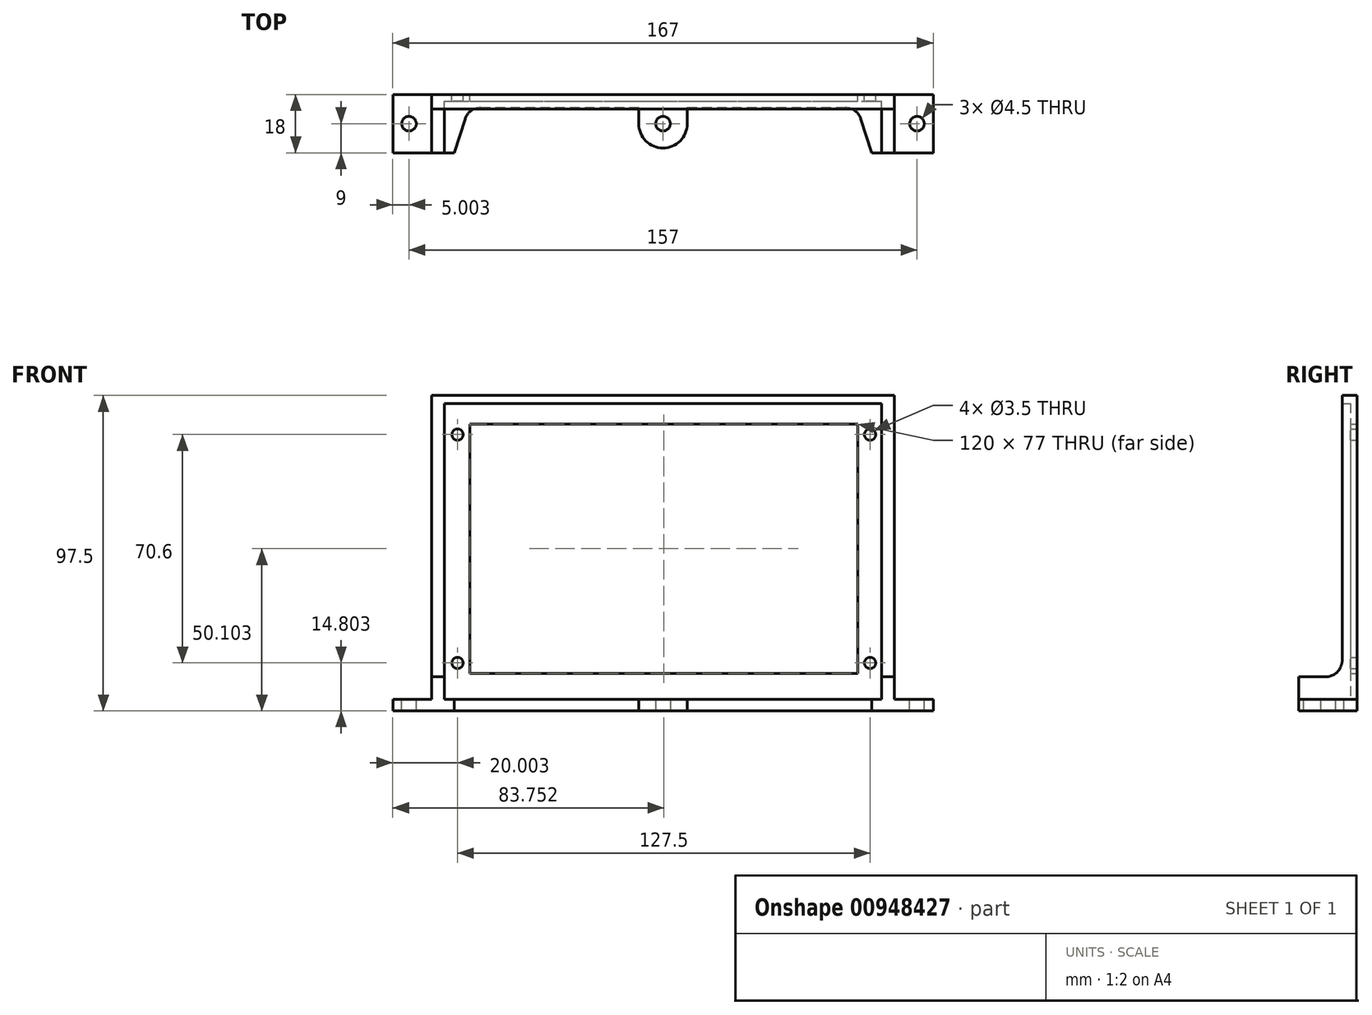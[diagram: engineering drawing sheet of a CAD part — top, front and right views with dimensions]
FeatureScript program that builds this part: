
annotation { "Feature Type Name" : "Feature", "Feature Type Description" : "" }
export const myFeature = defineFeature(function(context is Context, id is Id, definition is map)
    precondition{}
    {
        {
            var Q0;
            Q0=qCreatedBy(makeId("Front.planeOp"),FACE);
            var sketch = newSketch(context, id + "F0", { "sketchPlane" : qUnion([Q0])});
            skLineSegment(sketch, "E0.bottom", {"start": v(-17.88, 24.05) * mm, "end": v(102.12, 24.05) * mm});
            skLineSegment(sketch, "E0.top", {"start": v(-17.88, -52.95) * mm, "end": v(102.12, -52.95) * mm});
            skLineSegment(sketch, "E0.left", {"start": v(-17.88, 24.05) * mm, "end": v(-17.88, -52.95) * mm});
            skLineSegment(sketch, "E0.right", {"start": v(102.12, 24.05) * mm, "end": v(102.12, -52.95) * mm});
            skLineSegment(sketch, "E1.bottom", {"start": v(-25.63, 30.45) * mm, "end": v(109.37, 30.45) * mm});
            skLineSegment(sketch, "E1.top", {"start": v(-25.63, -59.55) * mm, "end": v(109.37, -59.55) * mm});
            skLineSegment(sketch, "E1.left", {"start": v(-25.63, 30.45) * mm, "end": v(-25.63, -59.55) * mm});
            skLineSegment(sketch, "E1.right", {"start": v(109.37, 30.45) * mm, "end": v(109.37, -59.55) * mm});
            skLineSegment(sketch, "E2.bottom", {"start": v(-21.63, 20.85) * mm, "end": v(105.87, 20.85) * mm, "construction": true});
            skLineSegment(sketch, "E2.top", {"start": v(-21.63, -49.75) * mm, "end": v(105.87, -49.75) * mm, "construction": true});
            skLineSegment(sketch, "E2.left", {"start": v(-21.63, 20.85) * mm, "end": v(-21.63, -49.75) * mm, "construction": true});
            skLineSegment(sketch, "E2.right", {"start": v(105.87, 20.85) * mm, "end": v(105.87, -49.75) * mm, "construction": true});
            skCircle(sketch, "E3", {"center": v(-21.63, 20.85) * mm, "radius": 1.75 * mm});
            skCircle(sketch, "E4", {"center": v(-21.63, -49.75) * mm, "radius": 1.75 * mm});
            skCircle(sketch, "E5", {"center": v(105.87, -49.75) * mm, "radius": 1.75 * mm});
            skCircle(sketch, "E6", {"center": v(105.87, 20.85) * mm, "radius": 1.75 * mm});
            skLineSegment(sketch, "E7.top", {"start": v(-29.63, -64.55) * mm, "end": v(113.37, -64.55) * mm});
            skLineSegment(sketch, "E8.top", {"start": v(-25.63, 30.45) * mm, "end": v(-29.63, 30.45) * mm});
            skLineSegment(sketch, "E8.left", {"start": v(-25.63, -59.55) * mm, "end": v(-25.63, 30.45) * mm});
            skLineSegment(sketch, "E8.right", {"start": v(-29.63, -64.55) * mm, "end": v(-29.63, 30.45) * mm});
            skLineSegment(sketch, "E9.bottom", {"start": v(109.37, 30.45) * mm, "end": v(113.37, 30.45) * mm});
            skLineSegment(sketch, "E9.left", {"start": v(109.37, 30.45) * mm, "end": v(109.37, -60.05) * mm});
            skLineSegment(sketch, "E9.right", {"start": v(113.37, 30.45) * mm, "end": v(113.37, -64.55) * mm});
            skPoint(sketch, "E7.right.start.orphan", {"position": v(122.02, -59.55) * mm});
            skPoint(sketch, "E10.orphan", {"position": v(-41.66, -59.55) * mm});
            skLineSegment(sketch, "E11", {"start": v(-17.88, -14.45) * mm, "end": v(102.12, -14.45) * mm, "construction": true});
            skPoint(sketch, "E12", {"position": v(-21.63, -14.45) * mm});
            skPoint(sketch, "E13", {"position": v(42.12, 20.85) * mm});
            skPoint(sketch, "E14", {"position": v(42.12, 24.05) * mm});
            skPoint(sketch, "E15", {"position": v(41.87, 30.45) * mm});
            skSolve(sketch);
        }
        {
            var Q0;
            Q0=makeQuery(id+"F0.imprint","IMPRINT",FACE,{"disambiguationData":[TD([[makeQuery(id+"F0.imprint","IMPRINT",EDGE,{"derivedFrom":sQuery(id+"F0.wireOp",EDGE,"E0.bottom")}),1.0]])]});
            extrude(context, id + "F1", {"entities" : qUnion([Q0]), "depth" : 2 * mm, "offsetDistance" : 25 * mm});
        }
        {
            var Q0;
            Q0=makeQuery(id+"F0.imprint","IMPRINT",FACE,{"disambiguationData":[TD([[makeQuery(id+"F0.imprint","IMPRINT",EDGE,{"derivedFrom":sQuery(id+"F0.wireOp",EDGE,"E8.bottom")}),-1.0]])]});
            var Q1;
            Q1=makeQuery(id+"F0.imprint","IMPRINT",FACE,{"disambiguationData":[TD([[makeQuery(id+"F0.imprint","IMPRINT",EDGE,{"derivedFrom":sQuery(id+"F0.wireOp",EDGE,"E1.top")}),-1.0]])]});
            var Q2;
            Q2=makeQuery(id+"F0.imprint","IMPRINT",FACE,{"disambiguationData":[TD([[makeQuery(id+"F0.imprint","IMPRINT",EDGE,{"derivedFrom":sQuery(id+"F0.wireOp",EDGE,"E1.top")}),-1.0]])]});
            extrude(context, id + "F2", {"entities" : qUnion([Q0, Q1, Q2]), "operationType" : NewBodyOperationType.ADD, "depth" : 18 * mm, "offsetDistance" : 25 * mm});
        }
        {
            var Q0;
            Q0=makeQuery(id+"F2.opExtrude","SWEPT_FACE",FACE,{"disambiguationData":[OSD([sQuery(id+"F0.wireOp",EDGE,"E7.top")])]});
            var sketch = newSketch(context, id + "F3", { "sketchPlane" : qUnion([Q0])});
            skLineSegment(sketch, "E16", {"start": v(-29.63, 9) * mm, "end": v(113.37, 9) * mm, "construction": true});
            skCircle(sketch, "E17", {"center": v(-9.63, 9) * mm, "radius": 2.25 * mm});
            skCircle(sketch, "E18", {"center": v(41.87, 9) * mm, "radius": 2.25 * mm});
            skCircle(sketch, "E19", {"center": v(93.37, 9) * mm, "radius": 2.25 * mm});
            skSolve(sketch);
        }
        {
            var Q0;
            Q0=makeQuery(id+"F3.imprint","IMPRINT",FACE,{"disambiguationData":[TD([[makeQuery(id+"F3.imprint","IMPRINT",EDGE,{"derivedFrom":sQuery(id+"F3.wireOp",EDGE,"E17")}),1.0]])]});
            var Q1;
            Q1=makeQuery(id+"F3.imprint","IMPRINT",FACE,{"disambiguationData":[TD([[makeQuery(id+"F3.imprint","IMPRINT",EDGE,{"derivedFrom":sQuery(id+"F3.wireOp",EDGE,"E18")}),1.0]])]});
            var Q2;
            Q2=makeQuery(id+"F3.imprint","IMPRINT",FACE,{"disambiguationData":[TD([[makeQuery(id+"F3.imprint","IMPRINT",EDGE,{"derivedFrom":sQuery(id+"F3.wireOp",EDGE,"E19")}),1.0]])]});
            extrude(context, id + "F4", {"entities" : qUnion([Q0, Q1, Q2]), "operationType" : NewBodyOperationType.REMOVE, "oppositeDirection" : true, "depth" : 25 * mm, "offsetDistance" : 25 * mm});
        }
        {
            var Q0;
            Q0=makeQuery(id+"F2.opExtrude","SWEPT_FACE",FACE,{"disambiguationData":[OSD([sQuery(id+"F0.wireOp",EDGE,"E1.top")])]});
            extrude(context, id + "F5", {"entities" : qUnion([Q0]), "operationType" : NewBodyOperationType.REMOVE, "oppositeDirection" : true, "depth" : 1.5 * mm, "offsetDistance" : 25 * mm});
        }
        {
            var Q0;
            Q0=makeQuery(id+"F2.opExtrude","SWEPT_FACE",FACE,{"disambiguationData":[OSD([sQuery(id+"F0.wireOp",EDGE,"E9.right")])]});
            var sketch = newSketch(context, id + "F6", { "sketchPlane" : qUnion([Q0])});
            skLineSegment(sketch, "E20", {"start": v(-18, -54.05) * mm, "end": v(-9.63, -54.05) * mm});
            skLineSegment(sketch, "E21", {"start": v(-4.5, 30.45) * mm, "end": v(-4.5, -48.35) * mm});
            skPoint(sketch, "E22.0", {"position": v(-2, 30.45) * mm});
            skPoint(sketch, "E23.0", {"position": v(-18, -61.05) * mm});
            skArc(sketch, "E24", {"start": v(-4.95, -50.82) * mm, "mid": v(-4.61, -49.6) * mm, "end": v(-4.5, -48.35) * mm});
            skPoint(sketch, "E25.visualSharp", {"position": v(-7.46, -54.05) * mm});
            skArc(sketch, "E25.filletArc", {"start": v(-9.63, -54.05) * mm, "mid": v(-6.79, -53.16) * mm, "end": v(-4.95, -50.82) * mm});
            skSolve(sketch);
        }
        {
            var Q0;
            {var subQ1=sQuery(id+"F6.wireOp",EDGE,"E20");Q0=makeQuery(id+"F6.imprint","IMPRINT",FACE,{"disambiguationData":[TD([[makeQuery(id+"F6.imprint","IMPRINT",EDGE,{"derivedFrom":subQ1}),1.0]])]});}
            extrude(context, id + "F7", {"entities" : qUnion([Q0]), "operationType" : NewBodyOperationType.REMOVE, "endBound" : BoundingType.THROUGH_ALL, "oppositeDirection" : true, "depth" : 25 * mm, "offsetDistance" : 25 * mm});
        }
        {
            var Q0;
            Q0=makeQuery(id+"F2.opExtrude","SWEPT_FACE",FACE,{"disambiguationData":[OSD([sQuery(id+"F0.wireOp",EDGE,"E7.top")])]});
            var sketch = newSketch(context, id + "F8", { "sketchPlane" : qUnion([Q0])});
            skLineSegment(sketch, "E26.bottom", {"start": v(113.37, 18) * mm, "end": v(125.37, 18) * mm});
            skLineSegment(sketch, "E26.top", {"start": v(113.37, 0) * mm, "end": v(125.37, 0) * mm});
            skLineSegment(sketch, "E26.left", {"start": v(113.37, 18) * mm, "end": v(113.37, 0) * mm});
            skLineSegment(sketch, "E26.right", {"start": v(125.37, 18) * mm, "end": v(125.37, 0) * mm});
            skLineSegment(sketch, "E27.bottom", {"start": v(-29.63, 0) * mm, "end": v(-41.63, 0) * mm});
            skLineSegment(sketch, "E27.top", {"start": v(-29.63, 18) * mm, "end": v(-41.63, 18) * mm});
            skLineSegment(sketch, "E27.left", {"start": v(-29.63, 0) * mm, "end": v(-29.63, 18) * mm});
            skLineSegment(sketch, "E27.right", {"start": v(-41.63, 0) * mm, "end": v(-41.63, 18) * mm});
            skSolve(sketch);
        }
        {
            var Q0;
            Q0=makeQuery(id+"F8.imprint","IMPRINT",FACE,{"disambiguationData":[TD([[makeQuery(id+"F8.imprint","IMPRINT",EDGE,{"derivedFrom":sQuery(id+"F8.wireOp",EDGE,"E27.bottom")}),-1.0]])]});
            var Q1;
            Q1=makeQuery(id+"F8.imprint","IMPRINT",FACE,{"disambiguationData":[TD([[makeQuery(id+"F8.imprint","IMPRINT",EDGE,{"derivedFrom":sQuery(id+"F8.wireOp",EDGE,"E26.bottom")}),-1.0]])]});
            var Q2;
            Q2=makeQuery(id+"F5.boolean.opBoolean","COPY",FACE,{"derivedFrom":makeQuery(id+"F5.opExtrude","CAP_FACE",FACE,{"disambiguationData":[OSD([sQuery(id+"F0.wireOp",EDGE,"E1.top")])],"isStart":false})});
            extrude(context, id + "F9", {"entities" : qUnion([Q0, Q1]), "operationType" : NewBodyOperationType.ADD, "endBound" : BoundingType.UP_TO_SURFACE, "oppositeDirection" : true, "depth" : 25 * mm, "endBoundEntityFace" : qUnion([Q2]), "offsetDistance" : 25 * mm});
        }
        {
            var Q0;
            Q0=makeQuery(id+"F9.opExtrude","CAP_FACE",FACE,{"disambiguationData":[OSD([sQuery(id+"F8.wireOp",EDGE,"E26.bottom"),sQuery(id+"F8.wireOp",EDGE,"E26.top"),sQuery(id+"F8.wireOp",EDGE,"E26.left"),sQuery(id+"F8.wireOp",EDGE,"E26.right")])],"isStart":false});
            var sketch = newSketch(context, id + "F10", { "sketchPlane" : qUnion([Q0])});
            skLineSegment(sketch, "E28", {"start": v(120.37, -18) * mm, "end": v(120.37, 0) * mm, "construction": true});
            skLineSegment(sketch, "E29", {"start": v(125.37, -9) * mm, "end": v(113.37, -8.7) * mm, "construction": true});
            skCircle(sketch, "E30", {"center": v(120.37, -9) * mm, "radius": 2.25 * mm});
            skLineSegment(sketch, "E31.0.0", {"start": v(-41.63, -18) * mm, "end": v(-29.63, -18) * mm});
            skLineSegment(sketch, "E31.0.1", {"start": v(-29.63, -18) * mm, "end": v(-29.63, 0) * mm});
            skLineSegment(sketch, "E31.0.2", {"start": v(-29.63, 0) * mm, "end": v(-41.63, 0) * mm});
            skLineSegment(sketch, "E31.0.3", {"start": v(-41.63, 0) * mm, "end": v(-41.63, -18) * mm});
            skLineSegment(sketch, "E32", {"start": v(-41.63, -9) * mm, "end": v(-29.63, -9) * mm, "construction": true});
            skLineSegment(sketch, "E33", {"start": v(-36.63, -18) * mm, "end": v(-36.63, 0) * mm, "construction": true});
            skCircle(sketch, "E34", {"center": v(-36.63, -9) * mm, "radius": 2.25 * mm});
            skSolve(sketch);
        }
        {
            var Q0;
            Q0=makeQuery(id+"F10.imprint","IMPRINT",FACE,{"disambiguationData":[TD([[makeQuery(id+"F10.imprint","IMPRINT",EDGE,{"derivedFrom":sQuery(id+"F10.wireOp",EDGE,"E34")}),1.0]])]});
            var Q1;
            Q1=makeQuery(id+"F10.imprint","IMPRINT",FACE,{"disambiguationData":[TD([[makeQuery(id+"F10.imprint","IMPRINT",EDGE,{"derivedFrom":sQuery(id+"F10.wireOp",EDGE,"E30")}),1.0]])]});
            extrude(context, id + "F11", {"entities" : qUnion([Q0, Q1]), "operationType" : NewBodyOperationType.REMOVE, "endBound" : BoundingType.THROUGH_ALL, "oppositeDirection" : true, "depth" : 25 * mm, "offsetDistance" : 25 * mm});
        }
        {
            var Q0;
            Q0=makeQuery(id+"F5.boolean.opBoolean","COPY",FACE,{"derivedFrom":makeQuery(id+"F5.opExtrude","CAP_FACE",FACE,{"disambiguationData":[OSD([sQuery(id+"F0.wireOp",EDGE,"E1.top")])],"isStart":false})});
            var sketch = newSketch(context, id + "F12", { "sketchPlane" : qUnion([Q0])});
            skLineSegment(sketch, "E35", {"start": v(41.87, -9) * mm, "end": v(41.87, -18) * mm, "construction": true});
            skLineSegment(sketch, "E36", {"start": v(-14.48, -4) * mm, "end": v(34.37, -4) * mm});
            skLineSegment(sketch, "E37", {"start": v(34.37, -9) * mm, "end": v(34.37, -4) * mm});
            skLineSegment(sketch, "E38", {"start": v(49.37, -9) * mm, "end": v(49.37, -4) * mm});
            skLineSegment(sketch, "E39", {"start": v(-22.63, -18) * mm, "end": v(-19.24, -7.47) * mm});
            skLineSegment(sketch, "E40", {"start": v(106.37, -18) * mm, "end": v(102.99, -7.47) * mm});
            skArc(sketch, "E41", {"start": v(34.37, -9) * mm, "mid": v(41.87, -16.5) * mm, "end": v(49.37, -9) * mm});
            skPoint(sketch, "E42.orphan", {"position": v(109.37, -4) * mm});
            skPoint(sketch, "E43.orphan", {"position": v(-25.63, -4) * mm});
            skPoint(sketch, "E44.visualSharp", {"position": v(-18.13, -4) * mm});
            skArc(sketch, "E44.filletArc", {"start": v(-14.48, -4) * mm, "mid": v(-17.43, -4.96) * mm, "end": v(-19.24, -7.47) * mm});
            skPoint(sketch, "E45.visualSharp", {"position": v(101.87, -4) * mm});
            skArc(sketch, "E45.filletArc", {"start": v(102.99, -7.47) * mm, "mid": v(101.17, -4.96) * mm, "end": v(98.23, -4) * mm});
            skLineSegment(sketch, "E46.trimOffspring", {"start": v(49.37, -4) * mm, "end": v(98.23, -4) * mm});
            skSolve(sketch);
        }
        {
            var Q0;
            Q0=makeQuery(id+"F12.imprint","IMPRINT",FACE,{"disambiguationData":[TD([[makeQuery(id+"F12.imprint","IMPRINT",EDGE,{"derivedFrom":sQuery(id+"F12.wireOp",EDGE,"E36")}),-1.0]])]});
            extrude(context, id + "F13", {"entities" : qUnion([Q0]), "operationType" : NewBodyOperationType.REMOVE, "endBound" : BoundingType.THROUGH_ALL, "oppositeDirection" : true, "depth" : 25 * mm, "offsetDistance" : 25 * mm});
        }
        {
            var Q0;
            Q0=makeQuery(id+"F2.boolean.opBoolean","MERGE",FACE,{"derivedFrom":[makeQuery(id+"F1.opExtrude","SWEPT_FACE",FACE,{"disambiguationData":[OSD([sQuery(id+"F0.wireOp",EDGE,"E1.bottom")])]}),makeQuery(id+"F2.opExtrude","SWEPT_FACE",FACE,{"disambiguationData":[OSD([sQuery(id+"F0.wireOp",EDGE,"E8.top")])]}),makeQuery(id+"F2.opExtrude","SWEPT_FACE",FACE,{"disambiguationData":[OSD([sQuery(id+"F0.wireOp",EDGE,"E9.bottom")])]})]});
            var sketch = newSketch(context, id + "F14", { "sketchPlane" : qUnion([Q0])});
            skLineSegment(sketch, "E47", {"start": v(-25.63, -4.5) * mm, "end": v(109.37, -4.5) * mm});
            skSolve(sketch);
        }
        {
            var Q0;
            Q0=makeQuery(id+"F14.imprint","IMPRINT",FACE,{"disambiguationData":[TD([[makeQuery(id+"F14.imprint","IMPRINT",EDGE,{"derivedFrom":sQuery(id+"F14.wireOp",EDGE,"E47")}),1.0]])]});
            var Q1;
            {var subQ4=sQuery(id+"F0.wireOp",EDGE,"E1.bottom");Q1=makeQuery(id+"F14.imprint","IMPRINT",FACE,{"disambiguationData":[TD([[makeQuery(id+"F14.imprint","IMPRINT",EDGE,{"derivedFrom":makeQuery(id+"F1.opExtrude","CAP_EDGE",EDGE,{"disambiguationData":[OSD([subQ4])],"isStart":false})}),1.0]])]});}
            extrude(context, id + "F15", {"entities" : qUnion([Q0, Q1]), "operationType" : NewBodyOperationType.ADD, "depth" : 2.5 * mm, "offsetDistance" : 25 * mm});
        }
    });
